# Revit family: Chair-Multi_Purpose-Allermuir-Elios-HD415
name_source: partatom
category: Furniture
revit_build: Autodesk Revit Architecture 2012 (Build: 20110309_2315(x64)
units: mm (PartAtom-declared; Revit-internal decimal feet)

## types (1)
- HD415
    04 CSI = 12 51 00
    95 CSI = 12510
    Arm = Plastic - Allermuir - Black
    Arm Height = 2' - 2"
    Assembly Code = E2020200
    Back = Plastic - Allermuir - Upholstery - LED - Red Off
    Brochure URL = http://www.allermuir.net
    CAD Blocks URL = http://www.allermuir.net
    Color Availability = See price list for material options
    Description = Side chair, plastic seat and back, no arms
    Fabric Spec Sheets = http://www.allermuir.net
    LEED Stats URL = http://www.allermuir.net
    Leg = Metal - Allermuir - Chrome - Polished
    Leg Base = Plastic - Allermuir - Black
    Manufacturer = Allermuir
    Manufacturer Fax = (419) 887 5805
    Model = HD415
    Overall Depth = 1' - 8"
    Overall Height = 2' - 8"
    Overall Width = 1' - 10 1/2"
    Plastic Arms in Black = No
    Plugin Data URL = http://products.ecoscorecard.com
    Pricing URL = http://www.allermuir.net
    Product Line = Elios
    Product Page URL = http://www.allermuir.net
    Seat Depth = 1' - 5 205/256"
    Seat Height = 1' - 6"
    Seat Width = 1' - 5 1/2"
    Seat or Base = Plastic - Allermuir - Upholstery - LED - Red Off
    Specifications URL = http://www.allermuir.net
    Stacks = Yes
    Subcategory = Multi-Purpose Line
    URL = http://www.allermuir.net
    Upholstered Back = No
    Upholstered Seat = No
    Weight = 15.0 lb
    ecoScorecard Product Page = http://products.ecoscorecard.com
    ecoScorecard_data = http://thesenatorgroup.ecoscorecard.com

## geometry (parser evidence)
native form markers: Sweep x4
no freeform markers — native parametric forms only
